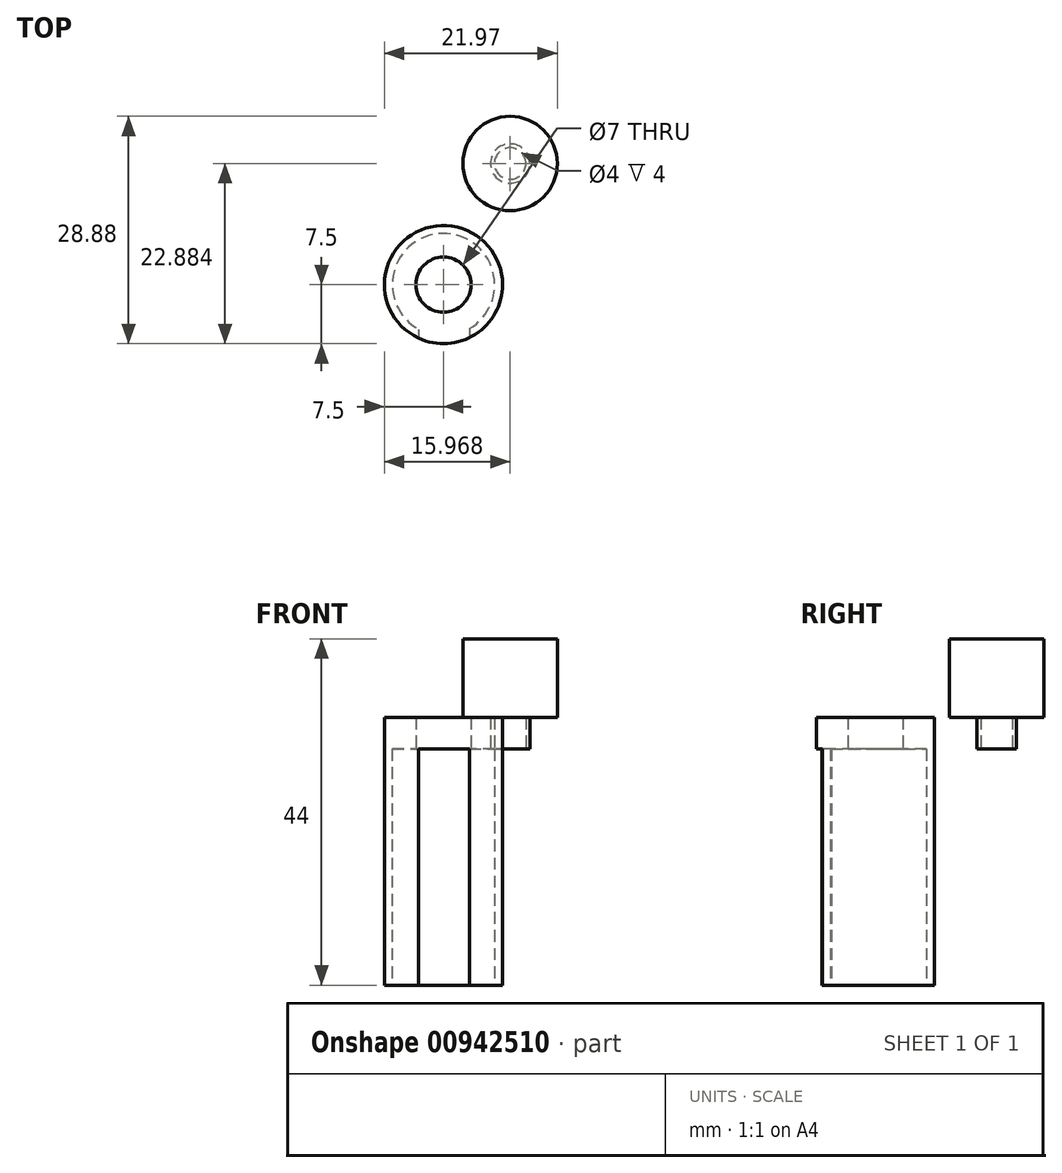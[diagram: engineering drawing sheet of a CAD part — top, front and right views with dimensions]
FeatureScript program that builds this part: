
annotation { "Feature Type Name" : "Feature", "Feature Type Description" : "" }
export const myFeature = defineFeature(function(context is Context, id is Id, definition is map)
    precondition{}
    {
        {
            var Q0;
            Q0=qCreatedBy(makeId("Top.planeOp"),FACE);
            var sketch = newSketch(context, id + "F0", { "sketchPlane" : qUnion([Q0])});
            skArc(sketch, "E0", {"start": v(3.28, -6.75) * mm, "mid": v(-0.07, 7.5) * mm, "end": v(-3.15, -6.8) * mm});
            skArc(sketch, "E1", {"start": v(3.29, -5.6) * mm, "mid": v(-0.08, 6.5) * mm, "end": v(-3.15, -5.68) * mm});
            skLineSegment(sketch, "E2", {"start": v(-3.15, -5.68) * mm, "end": v(-3.15, -6.8) * mm});
            skLineSegment(sketch, "E3", {"start": v(3.29, -5.6) * mm, "end": v(3.28, -6.75) * mm});
            skSolve(sketch);
        }
        {
            var Q0;
            Q0 = qSketchRegion(id + "F0", true);
            var Q1;
            Q1 = qSketchRegion(id + "F3", true);
            extrude(context, id + "F1", {"entities" : qUnion([Q0, Q1]), "depth" : 30 * mm, "offsetDistance" : 25 * mm});
        }
        {
            var Q0;
            Q0=qCreatedBy(makeId("Top.planeOp"),FACE);
            var Q1;
            Q1=sQuery(id+"FVVA0BDztVoJ6aG_1.wireOp",EDGE,"kQUGKYdO-F6O5-vBEh-TMmz-P9zsAZJyhf8Q");
            cPlane(context, id + "F2", {"entities" : qUnion([Q0, Q1]), "cplaneType" : CPlaneType.OFFSET, "offset" : 30 * mm, "width" : 150 * mm, "height" : 150 * mm});
        }
        {
            var Q0;
            Q0=qCreatedBy(id+"F2.planeOp",FACE);
            var sketch = newSketch(context, id + "F3", { "sketchPlane" : qUnion([Q0])});
            skCircle(sketch, "E4", {"center": v(0, 0) * mm, "radius": 7.5 * mm});
            skCircle(sketch, "E5", {"center": v(0, 0) * mm, "radius": 3.5 * mm});
            skSolve(sketch);
        }
        {
            var Q0;
            Q0=makeQuery(id+"F3.imprint","IMPRINT",FACE,{"disambiguationData":[TD([[makeQuery(id+"F3.imprint","IMPRINT",EDGE,{"derivedFrom":sQuery(id+"F3.wireOp",EDGE,"E4")}),1.0]])]});
            extrude(context, id + "F4", {"entities" : qUnion([Q0]), "operationType" : NewBodyOperationType.ADD, "depth" : 4 * mm, "offsetDistance" : 25 * mm});
        }
        {
            var Q0;
            Q0=qCreatedBy(id+"F2.planeOp",FACE);
            var sketch = newSketch(context, id + "F5", { "sketchPlane" : qUnion([Q0])});
            skCircle(sketch, "E6", {"center": v(8.47, 15.38) * mm, "radius": 2.5 * mm});
            skCircle(sketch, "E7", {"center": v(8.47, 15.38) * mm, "radius": 2 * mm});
            skSolve(sketch);
        }
        {
            var Q0;
            Q0 = qSketchRegion(id + "F5", true);
            var Q1;
            Q1=sQuery(id+"F5.wireOp",EDGE,"E6");
            extrude(context, id + "F6", {"entities" : qUnion([Q0]), "surfaceEntities" : qUnion([Q1]), "depth" : 4 * mm, "offsetDistance" : 25 * mm});
        }
        {
            var Q0;
            Q0=makeQuery(id+"F6.opExtrude","CAP_FACE",FACE,{"disambiguationData":[OSD([sQuery(id+"F5.wireOp",EDGE,"E6"),sQuery(id+"F5.wireOp",EDGE,"E7")])],"isStart":false});
            var sketch = newSketch(context, id + "F7", { "sketchPlane" : qUnion([Q0])});
            skCircle(sketch, "E8", {"center": v(8.47, 15.38) * mm, "radius": 6 * mm});
            skSolve(sketch);
        }
        {
            var Q0;
            Q0 = qSketchRegion(id + "F7", true);
            extrude(context, id + "F8", {"entities" : qUnion([Q0]), "operationType" : NewBodyOperationType.ADD, "depth" : 10 * mm, "offsetDistance" : 25 * mm});
        }
    });
